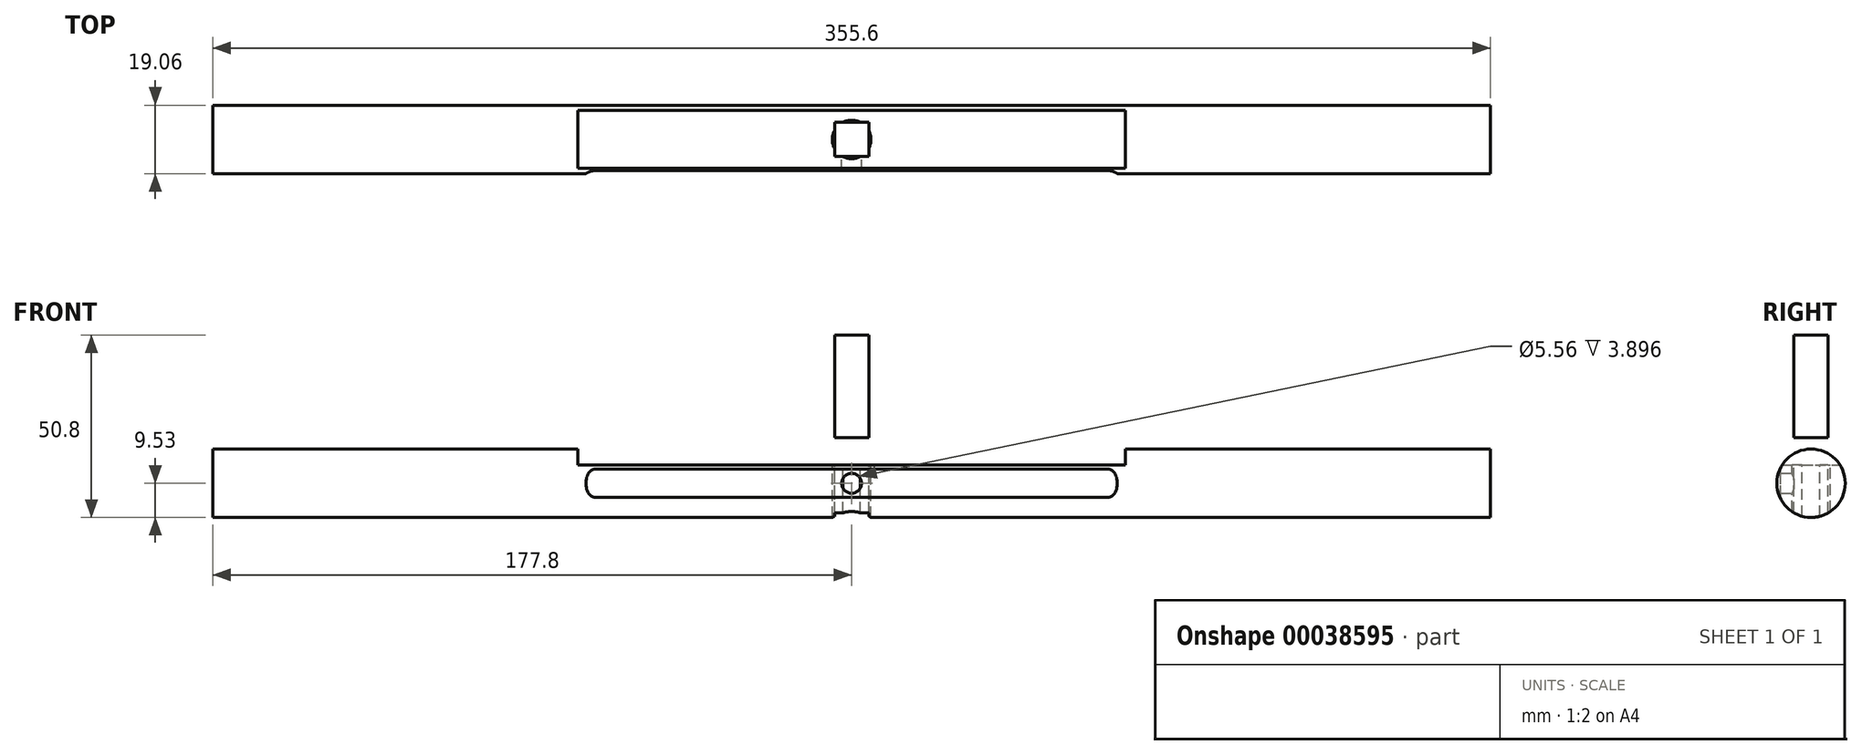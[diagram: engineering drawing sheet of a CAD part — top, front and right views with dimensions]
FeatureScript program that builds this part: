
annotation { "Feature Type Name" : "Feature", "Feature Type Description" : "" }
export const myFeature = defineFeature(function(context is Context, id is Id, definition is map)
    precondition{}
    {
        {
            var Q0;
            Q0=qCreatedBy(makeId("Front.planeOp"),FACE);
            var sketch = newSketch(context, id + "F0", { "sketchPlane" : qUnion([Q0])});
            skCircle(sketch, "E0", {"center": v(0, 0) * mm, "radius": 2.78 * mm});
            skSolve(sketch);
        }
        {
            var Q0;
            Q0=qCreatedBy(makeId("Top.planeOp"),FACE);
            var sketch = newSketch(context, id + "F1", { "sketchPlane" : qUnion([Q0])});
            skLineSegment(sketch, "E1.bottom", {"start": v(4.76, 4.76) * mm, "end": v(-4.76, 4.76) * mm});
            skLineSegment(sketch, "E1.top", {"start": v(4.76, -4.76) * mm, "end": v(-4.76, -4.76) * mm});
            skLineSegment(sketch, "E1.left", {"start": v(4.76, 4.76) * mm, "end": v(4.76, -4.76) * mm});
            skLineSegment(sketch, "E1.right", {"start": v(-4.76, 4.76) * mm, "end": v(-4.76, -4.76) * mm});
            skPoint(sketch, "E1.middle", {"position": v(0, 0) * mm});
            skSolve(sketch);
        }
        {
            var Q0;
            Q0=qCreatedBy(makeId("Top.planeOp"),FACE);
            var sketch = newSketch(context, id + "F2", { "sketchPlane" : qUnion([Q0])});
            skCircle(sketch, "E2", {"center": v(0, 0) * mm, "radius": 5.36 * mm});
            skCircle(sketch, "E3", {"center": v(0, 0) * mm, "radius": 6.35 * mm, "construction": true});
            skSolve(sketch);
        }
        {
            var Q0;
            Q0 = qSketchRegion(id + "F1", true);
            extrude(context, id + "F3", {"entities" : qUnion([Q0]), "depth" : 41.27 * mm, "hasSecondDirection" : true, "secondDirectionOppositeDirection" : true, "secondDirectionDepth" : 12.7 * mm});
        }
        {
            var Q0;
            Q0=qCreatedBy(makeId("Right.planeOp"),FACE);
            var sketch = newSketch(context, id + "F4", { "sketchPlane" : qUnion([Q0])});
            skCircle(sketch, "E4", {"center": v(0, 0) * mm, "radius": 9.53 * mm});
            skLineSegment(sketch, "E5", {"start": v(-8.06, 5.08) * mm, "end": v(8.06, 5.08) * mm});
            skLineSegment(sketch, "E6", {"start": v(-8.66, 3.97) * mm, "end": v(-8.66, -3.97) * mm});
            skSolve(sketch);
        }
        {
            var Q0;
            {var subQ0=sQuery(id+"F4.wireOp",EDGE,"E5");Q0=makeQuery(id+"F4.imprint","IMPRINT",FACE,{"disambiguationData":[TD([[makeQuery(id+"F4.imprint","IMPRINT",EDGE,{"derivedFrom":subQ0}),-1.0]])]});}
            extrude(context, id + "F5", {"entities" : qUnion([Q0]), "depth" : 76.2 * mm});
        }
        {
            var Q0;
            Q0 = qSketchRegion(id + "F4", true);
            extrude(context, id + "F6", {"entities" : qUnion([Q0]), "operationType" : NewBodyOperationType.ADD, "depth" : 177.8 * mm, "hasSecondDirection" : true, "secondDirectionOppositeDirection" : false, "secondDirectionDepth" : 76.2 * mm});
        }
        {
            var Q0;
            Q0=makeQuery(id+"F5.opExtrude","CAP_EDGE",EDGE,{"disambiguationData":[OSD([sQuery(id+"F4.wireOp",EDGE,"E5")])],"isStart":false});
            var Q1;
            Q1=makeQuery(id+"F5.opExtrude","CAP_EDGE",EDGE,{"disambiguationData":[OSD([sQuery(id+"F4.wireOp",EDGE,"E6")])],"isStart":false});
            fillet(context, id + "F7", {"entities" : qUnion([Q0, Q1]), "radius" : 5.08 * mm, "tangentPropagation" : true, "allowEdgeOverflow" : false});
        }
        {
            var Q0;
            Q0=makeQuery(id+"F5.opExtrude","SWEPT_BODY",BODY,{"disambiguationData":[OSD([sQuery(id+"F4.wireOp",EDGE,"E4"),sQuery(id+"F4.wireOp",EDGE,"E5"),sQuery(id+"F4.wireOp",EDGE,"E6")])]});
            var Q1;
            Q1=qCreatedBy(makeId("Right.planeOp"),FACE);
            mirror(context, id + "F8", {"operationType" : NewBodyOperationType.ADD, "entities" : qUnion([Q0]), "mirrorPlane" : qUnion([Q1])});
        }
        {
            var Q0;
            Q0 = qSketchRegion(id + "F2", true);
            extrude(context, id + "F9", {"entities" : qUnion([Q0]), "operationType" : NewBodyOperationType.REMOVE, "endBound" : BoundingType.SYMMETRIC, "oppositeDirection" : true, "depth" : 25.4 * mm});
        }
        {
            var Q0;
            Q0 = qSketchRegion(id + "F1", true);
            extrude(context, id + "F10", {"entities" : qUnion([Q0]), "operationType" : NewBodyOperationType.REMOVE, "endBound" : BoundingType.SYMMETRIC, "oppositeDirection" : true, "depth" : 25.4 * mm});
        }
        {
            var Q0;
            Q0 = qSketchRegion(id + "F0", true);
            extrude(context, id + "F11", {"entities" : qUnion([Q0]), "operationType" : NewBodyOperationType.REMOVE, "depth" : 25.4 * mm});
        }
    });
